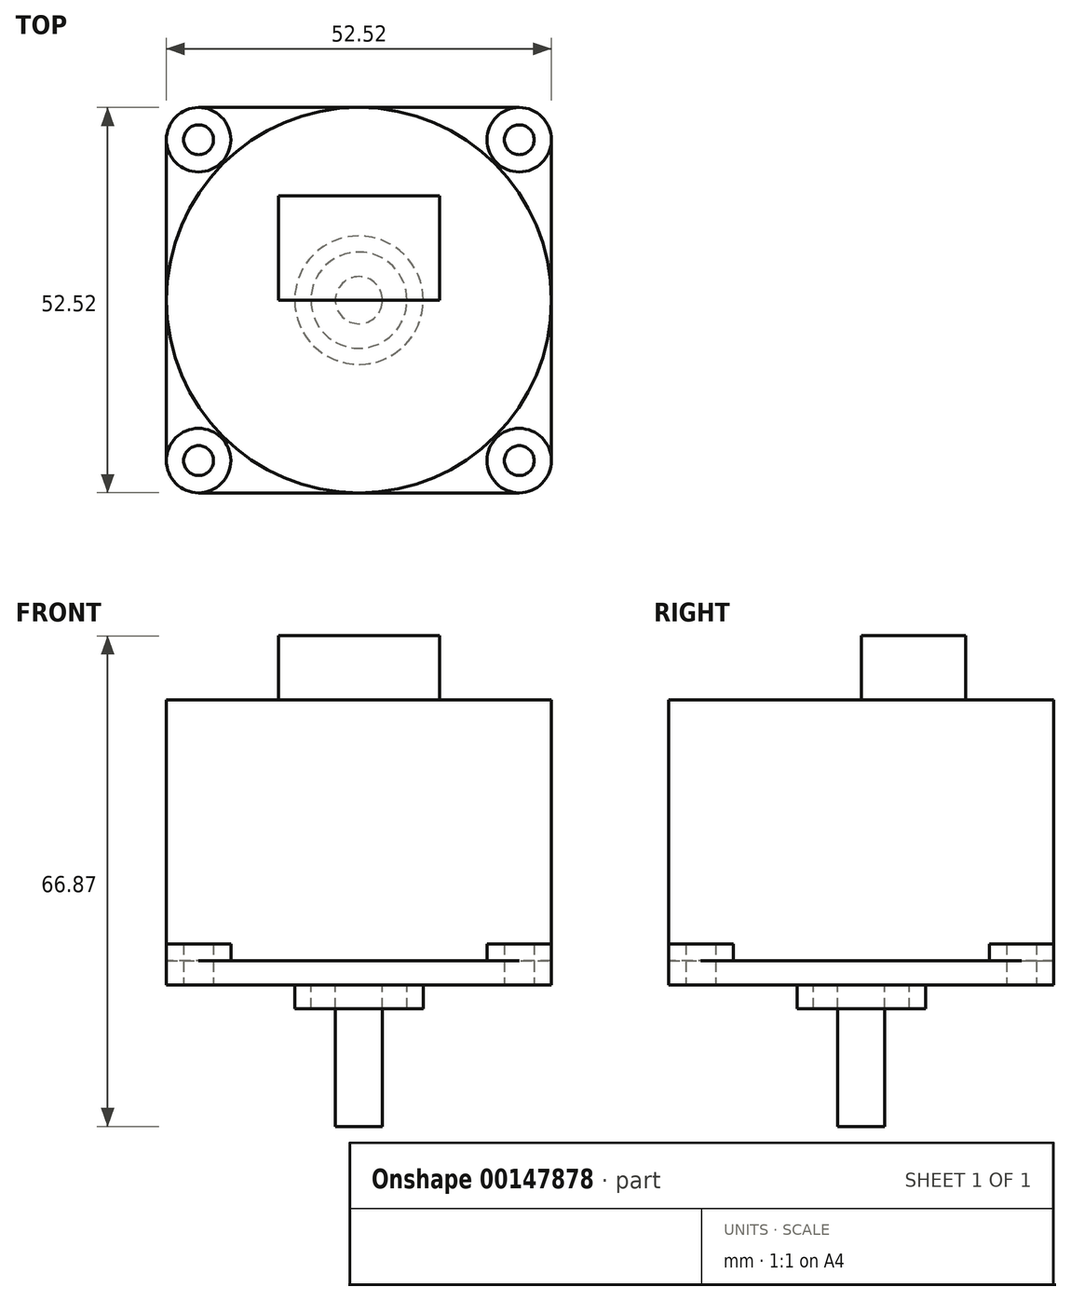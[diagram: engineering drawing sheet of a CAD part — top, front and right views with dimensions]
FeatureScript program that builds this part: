
annotation { "Feature Type Name" : "Feature", "Feature Type Description" : "" }
export const myFeature = defineFeature(function(context is Context, id is Id, definition is map)
    precondition{}
    {
        {
            var Q0;
            Q0=qCreatedBy(makeId("Top.planeOp"),FACE);
            var sketch = newSketch(context, id + "F0", { "sketchPlane" : qUnion([Q0])});
            skLineSegment(sketch, "E0.bottom", {"start": v(21.87, -21.87) * mm, "end": v(-21.87, -21.87) * mm, "construction": true});
            skLineSegment(sketch, "E0.top", {"start": v(21.87, 21.87) * mm, "end": v(-21.87, 21.87) * mm, "construction": true});
            skLineSegment(sketch, "E0.left", {"start": v(21.87, -21.87) * mm, "end": v(21.87, 21.87) * mm, "construction": true});
            skLineSegment(sketch, "E0.right", {"start": v(-21.87, -21.87) * mm, "end": v(-21.87, 21.87) * mm, "construction": true});
            skPoint(sketch, "E0.middle", {"position": v(0, 0) * mm});
            skLineSegment(sketch, "E1.bottom", {"start": v(26.26, -26.26) * mm, "end": v(-26.26, -26.26) * mm});
            skLineSegment(sketch, "E1.top", {"start": v(26.26, 26.26) * mm, "end": v(-26.26, 26.26) * mm});
            skLineSegment(sketch, "E1.left", {"start": v(26.26, -26.26) * mm, "end": v(26.26, 26.26) * mm});
            skLineSegment(sketch, "E1.right", {"start": v(-26.26, -26.26) * mm, "end": v(-26.26, 26.26) * mm});
            skCircle(sketch, "E2", {"center": v(21.87, 21.87) * mm, "radius": 2.03 * mm});
            skCircle(sketch, "E3", {"center": v(-21.87, 21.87) * mm, "radius": 2.03 * mm});
            skCircle(sketch, "E4", {"center": v(-21.87, -21.87) * mm, "radius": 2.03 * mm});
            skCircle(sketch, "E5", {"center": v(21.87, -21.87) * mm, "radius": 2.03 * mm});
            skSolve(sketch);
        }
        {
            var Q0;
            Q0=qSketchRegion(id+"F0",true);
            extrude(context, id + "F1", {"entities" : qUnion([Q0]), "depth" : 3.25 * mm});
        }
        {
            var Q0;
            Q0=makeQuery(id+"F1.opExtrude","CAP_FACE",FACE,{"disambiguationData":[OSD([sQuery(id+"F0.wireOp",EDGE,"E1.bottom"),sQuery(id+"F0.wireOp",EDGE,"E1.top"),sQuery(id+"F0.wireOp",EDGE,"E1.left"),sQuery(id+"F0.wireOp",EDGE,"E1.right"),sQuery(id+"F0.wireOp",EDGE,"E2"),sQuery(id+"F0.wireOp",EDGE,"E3"),sQuery(id+"F0.wireOp",EDGE,"E4"),sQuery(id+"F0.wireOp",EDGE,"E5")])],"isStart":false});
            var sketch = newSketch(context, id + "F2", { "sketchPlane" : qUnion([Q0])});
            skCircle(sketch, "E6", {"center": v(0, 0) * mm, "radius": 26.26 * mm});
            skSolve(sketch);
        }
        {
            var Q0;
            Q0=qSketchRegion(id+"F2",true);
            extrude(context, id + "F3", {"entities" : qUnion([Q0]), "operationType" : NewBodyOperationType.ADD, "depth" : 35.56 * mm});
        }
        {
            var Q0;
            Q0=makeQuery(id+"F3.opExtrude","CAP_FACE",FACE,{"disambiguationData":[OSD([sQuery(id+"F2.wireOp",EDGE,"E6")])],"isStart":false});
            var sketch = newSketch(context, id + "F4", { "sketchPlane" : qUnion([Q0])});
            skLineSegment(sketch, "E7.bottom", {"start": v(-10.99, 0) * mm, "end": v(10.99, 0) * mm});
            skLineSegment(sketch, "E7.top", {"start": v(-10.99, 14.22) * mm, "end": v(10.99, 14.22) * mm});
            skLineSegment(sketch, "E7.left", {"start": v(-10.99, 0) * mm, "end": v(-10.99, 14.22) * mm});
            skLineSegment(sketch, "E7.right", {"start": v(10.99, 0) * mm, "end": v(10.99, 14.22) * mm});
            skPoint(sketch, "E8", {"position": v(0, 0) * mm});
            skSolve(sketch);
        }
        {
            var Q0;
            Q0=qSketchRegion(id+"F4",true);
            extrude(context, id + "F5", {"entities" : qUnion([Q0]), "operationType" : NewBodyOperationType.ADD, "depth" : 8.76 * mm});
        }
        {
            var Q0;
            Q0=makeQuery(id+"F1.opExtrude","SWEPT_EDGE",EDGE,{"disambiguationData":[OSD([sQuery(id+"F0.wireOp",EDGE,"E1.bottom"),sQuery(id+"F0.wireOp",EDGE,"E1.right")])]});
            var Q1;
            Q1=makeQuery(id+"F1.opExtrude","SWEPT_EDGE",EDGE,{"disambiguationData":[OSD([sQuery(id+"F0.wireOp",EDGE,"E1.bottom"),sQuery(id+"F0.wireOp",EDGE,"E1.left")])]});
            var Q2;
            Q2=makeQuery(id+"F1.opExtrude","SWEPT_EDGE",EDGE,{"disambiguationData":[OSD([sQuery(id+"F0.wireOp",EDGE,"E1.top"),sQuery(id+"F0.wireOp",EDGE,"E1.left")])]});
            var Q3;
            Q3=makeQuery(id+"F1.opExtrude","SWEPT_EDGE",EDGE,{"disambiguationData":[OSD([sQuery(id+"F0.wireOp",EDGE,"E1.top"),sQuery(id+"F0.wireOp",EDGE,"E1.right")])]});
            fillet(context, id + "F6", {"entities" : qUnion([Q0, Q1, Q2, Q3]), "radius" : 4.4 * mm, "tangentPropagation" : true, "allowEdgeOverflow" : false});
        }
        {
            var Q0;
            {var subQ0=sQuery(id+"F0.wireOp",EDGE,"E1.right");var subQ1=sQuery(id+"F0.wireOp",EDGE,"E4");var subQ2=sQuery(id+"F0.wireOp",EDGE,"E1.bottom");var subQ3=makeQuery(id+"F1.opExtrude","CAP_FACE",FACE,{"disambiguationData":[OSD([subQ2,sQuery(id+"F0.wireOp",EDGE,"E1.top"),sQuery(id+"F0.wireOp",EDGE,"E1.left"),subQ0,sQuery(id+"F0.wireOp",EDGE,"E2"),sQuery(id+"F0.wireOp",EDGE,"E3"),subQ1,sQuery(id+"F0.wireOp",EDGE,"E5")])],"isStart":false});Q0=makeQuery(id+"F3.boolean.opBoolean","SPLIT",FACE,{"disambiguationData":[TD([makeQuery(id+"F1.opExtrude","SWEPT_FACE",FACE,{"disambiguationData":[OSD([subQ1])]})])],"derivedFrom":subQ3});}
            var sketch = newSketch(context, id + "F7", { "sketchPlane" : qUnion([Q0])});
            skCircle(sketch, "E9", {"center": v(-21.87, -21.87) * mm, "radius": 4.4 * mm});
            skCircle(sketch, "E10", {"center": v(21.87, -21.87) * mm, "radius": 4.4 * mm});
            skCircle(sketch, "E11", {"center": v(-21.87, -21.87) * mm, "radius": 2.03 * mm});
            skCircle(sketch, "E12", {"center": v(21.87, -21.87) * mm, "radius": 2.03 * mm});
            skCircle(sketch, "E13", {"center": v(-21.87, 21.87) * mm, "radius": 4.4 * mm});
            skCircle(sketch, "E14", {"center": v(21.87, 21.87) * mm, "radius": 4.4 * mm});
            skCircle(sketch, "E15", {"center": v(-21.87, 21.87) * mm, "radius": 2.03 * mm});
            skCircle(sketch, "E16", {"center": v(21.87, 21.87) * mm, "radius": 2.03 * mm});
            skSolve(sketch);
        }
        {
            var Q0;
            Q0=qSketchRegion(id+"F7",true);
            extrude(context, id + "F8", {"entities" : qUnion([Q0]), "operationType" : NewBodyOperationType.ADD, "depth" : 2.34 * mm});
        }
        {
            var Q0;
            Q0=makeQuery(id+"F1.opExtrude","CAP_FACE",FACE,{"disambiguationData":[OSD([sQuery(id+"F0.wireOp",EDGE,"E1.bottom"),sQuery(id+"F0.wireOp",EDGE,"E1.top"),sQuery(id+"F0.wireOp",EDGE,"E1.left"),sQuery(id+"F0.wireOp",EDGE,"E1.right"),sQuery(id+"F0.wireOp",EDGE,"E2"),sQuery(id+"F0.wireOp",EDGE,"E3"),sQuery(id+"F0.wireOp",EDGE,"E4"),sQuery(id+"F0.wireOp",EDGE,"E5")])],"isStart":true});
            var sketch = newSketch(context, id + "F9", { "sketchPlane" : qUnion([Q0])});
            skCircle(sketch, "E17", {"center": v(0, 0) * mm, "radius": 3.21 * mm});
            skSolve(sketch);
        }
        {
            var Q0;
            Q0=qSketchRegion(id+"F9",true);
            extrude(context, id + "F10", {"entities" : qUnion([Q0]), "operationType" : NewBodyOperationType.ADD, "depth" : 19.3 * mm});
        }
        {
            var Q0;
            Q0=makeQuery(id+"F1.opExtrude","CAP_FACE",FACE,{"disambiguationData":[OSD([sQuery(id+"F0.wireOp",EDGE,"E1.bottom"),sQuery(id+"F0.wireOp",EDGE,"E1.top"),sQuery(id+"F0.wireOp",EDGE,"E1.left"),sQuery(id+"F0.wireOp",EDGE,"E1.right"),sQuery(id+"F0.wireOp",EDGE,"E2"),sQuery(id+"F0.wireOp",EDGE,"E3"),sQuery(id+"F0.wireOp",EDGE,"E4"),sQuery(id+"F0.wireOp",EDGE,"E5")])],"isStart":true});
            var sketch = newSketch(context, id + "F11", { "sketchPlane" : qUnion([Q0])});
            skCircle(sketch, "E18", {"center": v(0, 0) * mm, "radius": 6.55 * mm});
            skCircle(sketch, "E19", {"center": v(0, 0) * mm, "radius": 8.76 * mm});
            skSolve(sketch);
        }
        {
            var Q0;
            Q0=qSketchRegion(id+"F11",true);
            extrude(context, id + "F12", {"entities" : qUnion([Q0]), "operationType" : NewBodyOperationType.ADD, "depth" : 3.28 * mm});
        }
    });
